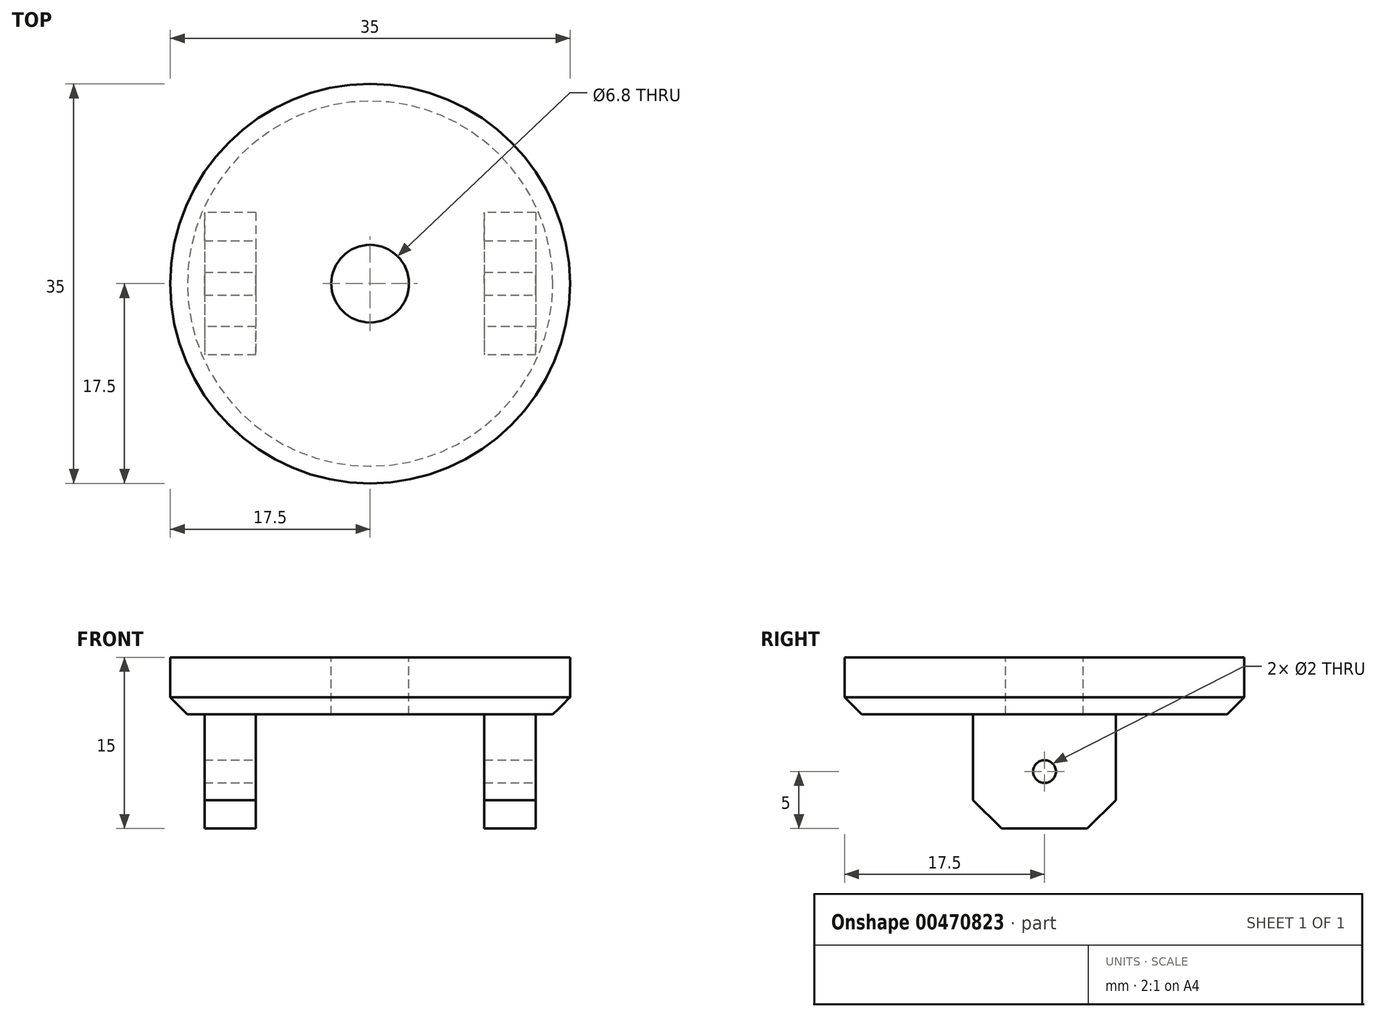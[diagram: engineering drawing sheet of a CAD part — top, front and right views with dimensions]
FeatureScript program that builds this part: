
annotation { "Feature Type Name" : "Feature", "Feature Type Description" : "" }
export const myFeature = defineFeature(function(context is Context, id is Id, definition is map)
    precondition{}
    {
        {
            var Q0;
            Q0=qCreatedBy(makeId("Top.planeOp"),FACE);
            var sketch = newSketch(context, id + "F0", { "sketchPlane" : qUnion([Q0])});
            skLineSegment(sketch, "E0.left", {"start": v(25, -7.7) * mm, "end": v(25, 7.7) * mm});
            skLineSegment(sketch, "E0.right", {"start": v(-25, -7.7) * mm, "end": v(-25, 7.7) * mm});
            skPoint(sketch, "E0.middle", {"position": v(0, 0) * mm});
            skEllipticalArc(sketch, "E1", {});
            skPoint(sketch, "E2.visualSharp", {"position": v(-25, 12.78) * mm});
            skArc(sketch, "E2.filletArc", {"start": v(-19.86, 15.83) * mm, "mid": v(-23.6, 12.5) * mm, "end": v(-25, 7.7) * mm});
            skArc(sketch, "E3.filletArc", {"start": v(-25, -7.7) * mm, "mid": v(-23.6, -12.5) * mm, "end": v(-19.86, -15.83) * mm});
            skEllipticalArc(sketch, "E4.trimOffspring", {});
            skPoint(sketch, "E5.visualSharp", {"position": v(25, 12.78) * mm});
            skArc(sketch, "E5.filletArc", {"start": v(25, 7.7) * mm, "mid": v(23.6, 12.5) * mm, "end": v(19.86, 15.83) * mm});
            skPoint(sketch, "E6.visualSharp", {"position": v(25, -12.78) * mm});
            skArc(sketch, "E6.filletArc", {"start": v(19.86, -15.83) * mm, "mid": v(23.6, -12.5) * mm, "end": v(25, -7.7) * mm});
            const initialGuessF0  = {"E1": [0, 0, 1, 0, 0.0325, 0.02, 4.054867696901255, 5.3699102638681255], "E4.trimOffspring": [0, 0, 1, 0, 0.0325, 0.02, 0.913275043311461, 2.2283176102783337]};
            skSetInitialGuess(sketch, initialGuessF0);
            skSolve(sketch);
        }
        {
            var Q0;
            Q0=makeQuery(id+"F0.imprint","IMPRINT",FACE,{"disambiguationData":[TD([[makeQuery(id+"F0.imprint","IMPRINT",EDGE,{"derivedFrom":sQuery(id+"F0.wireOp",EDGE,"E0.left")}),1.0]])]});
            extrude(context, id + "F1", {"entities" : qUnion([Q0]), "depth" : 5 * mm});
        }
        {
            var Q0;
            Q0=makeQuery(id+"F1.opExtrude","CAP_FACE",FACE,{"disambiguationData":[OSD([sQuery(id+"F0.wireOp",EDGE,"E0.left"),sQuery(id+"F0.wireOp",EDGE,"E0.right"),sQuery(id+"F0.wireOp",EDGE,"E1"),sQuery(id+"F0.wireOp",EDGE,"E2.filletArc"),sQuery(id+"F0.wireOp",EDGE,"E3.filletArc"),sQuery(id+"F0.wireOp",EDGE,"E4.trimOffspring"),sQuery(id+"F0.wireOp",EDGE,"E5.filletArc"),sQuery(id+"F0.wireOp",EDGE,"E6.filletArc")])],"isStart":true});
            var sketch = newSketch(context, id + "F2", { "sketchPlane" : qUnion([Q0])});
            skLineSegment(sketch, "E7.bottom", {"start": v(14.5, -6.25) * mm, "end": v(10, -6.25) * mm});
            skLineSegment(sketch, "E7.top", {"start": v(14.5, 6.25) * mm, "end": v(10, 6.25) * mm});
            skLineSegment(sketch, "E7.left", {"start": v(14.5, -6.25) * mm, "end": v(14.5, 6.25) * mm});
            skLineSegment(sketch, "E7.right", {"start": v(-14.5, -6.25) * mm, "end": v(-14.5, 6.25) * mm});
            skPoint(sketch, "E7.middle", {"position": v(0, 0) * mm});
            skLineSegment(sketch, "E8.left", {"start": v(10, -6.25) * mm, "end": v(10, 6.25) * mm});
            skLineSegment(sketch, "E8.right", {"start": v(-10, -6.25) * mm, "end": v(-10, 6.25) * mm});
            skLineSegment(sketch, "E9.trimOffspring", {"start": v(-10, 6.25) * mm, "end": v(-14.5, 6.25) * mm});
            skLineSegment(sketch, "E10.trimOffspring", {"start": v(-10, -6.25) * mm, "end": v(-14.5, -6.25) * mm});
            skSolve(sketch);
        }
        {
            var Q0;
            Q0=makeQuery(id+"F1.opExtrude","CAP_EDGE",EDGE,{"disambiguationData":[OSD([sQuery(id+"F0.wireOp",EDGE,"E1")])],"isStart":true});
            var Q1;
            Q1=makeQuery(id+"FL3o96M6EoHQmEN_1.opExtrude","CAP_FACE",FACE,{"disambiguationData":[OSD([sQuery(id+"F2.wireOp",EDGE,"E7.bottom"),sQuery(id+"F2.wireOp",EDGE,"E7.top"),sQuery(id+"F2.wireOp",EDGE,"E7.left"),sQuery(id+"F2.wireOp",EDGE,"E7.right")])],"isStart":false});
            chamfer(context, id + "F3", {"entities" : qUnion([Q0, Q1]), "width" : 1 * mm, "tangentPropagation" : true});
        }
        {
            var Q0;
            Q0 = qSketchRegion(id + "F2", true);
            extrude(context, id + "F4", {"entities" : qUnion([Q0]), "operationType" : NewBodyOperationType.ADD, "depth" : 10 * mm});
        }
        {
            var Q0;
            Q0=makeQuery(id+"F4.opExtrude","CAP_EDGE",EDGE,{"disambiguationData":[OSD([sQuery(id+"F2.wireOp",EDGE,"E9.trimOffspring")])],"isStart":false});
            var Q1;
            Q1=makeQuery(id+"F4.opExtrude","CAP_EDGE",EDGE,{"disambiguationData":[OSD([sQuery(id+"F2.wireOp",EDGE,"E7.top")])],"isStart":false});
            var Q2;
            Q2=makeQuery(id+"F4.opExtrude","CAP_EDGE",EDGE,{"disambiguationData":[OSD([sQuery(id+"F2.wireOp",EDGE,"E10.trimOffspring")])],"isStart":false});
            var Q3;
            Q3=makeQuery(id+"F4.opExtrude","CAP_EDGE",EDGE,{"disambiguationData":[OSD([sQuery(id+"F2.wireOp",EDGE,"E7.bottom")])],"isStart":false});
            chamfer(context, id + "F5", {"entities" : qUnion([Q0, Q1, Q2, Q3]), "width" : 2.5 * mm, "tangentPropagation" : true});
        }
        {
            var Q0;
            Q0=makeQuery(id+"F4.opExtrude","SWEPT_FACE",FACE,{"disambiguationData":[OSD([sQuery(id+"F2.wireOp",EDGE,"E7.left")])]});
            var sketch = newSketch(context, id + "F6", { "sketchPlane" : qUnion([Q0])});
            skCircle(sketch, "E11", {"center": v(0, -5) * mm, "radius": 1 * mm});
            skSolve(sketch);
        }
        {
            var Q0;
            Q0 = qSketchRegion(id + "F6", true);
            extrude(context, id + "F7", {"entities" : qUnion([Q0]), "operationType" : NewBodyOperationType.REMOVE, "endBound" : BoundingType.THROUGH_ALL, "oppositeDirection" : true, "depth" : 25 * mm});
        }
        {
            var Q0;
            Q0=makeQuery(id+"F1.opExtrude","CAP_FACE",FACE,{"disambiguationData":[OSD([sQuery(id+"F0.wireOp",EDGE,"E0.left"),sQuery(id+"F0.wireOp",EDGE,"E0.right"),sQuery(id+"F0.wireOp",EDGE,"E1"),sQuery(id+"F0.wireOp",EDGE,"E2.filletArc"),sQuery(id+"F0.wireOp",EDGE,"E3.filletArc"),sQuery(id+"F0.wireOp",EDGE,"E4.trimOffspring"),sQuery(id+"F0.wireOp",EDGE,"E5.filletArc"),sQuery(id+"F0.wireOp",EDGE,"E6.filletArc")])],"isStart":false});
            var sketch = newSketch(context, id + "F8", { "sketchPlane" : qUnion([Q0])});
            skCircle(sketch, "E12", {"center": v(0, 0) * mm, "radius": 17.5 * mm});
            skCircle(sketch, "E13", {"center": v(0, 0) * mm, "radius": 39.59 * mm});
            skSolve(sketch);
        }
        {
            var Q0;
            Q0=makeQuery(id+"F8.imprint","IMPRINT",FACE,{"disambiguationData":[TD([[makeQuery(id+"F8.imprint","IMPRINT",EDGE,{"derivedFrom":sQuery(id+"F8.wireOp",EDGE,"E12")}),-1.0]])]});
            var Q1;
            Q1=makeQuery(id+"F8.imprint","IMPRINT",FACE,{"disambiguationData":[TD([[makeQuery(id+"F8.imprint","IMPRINT",EDGE,{"derivedFrom":sQuery(id+"F8.wireOp",EDGE,"E13")}),1.0]])]});
            extrude(context, id + "F9", {"entities" : qUnion([Q0, Q1]), "operationType" : NewBodyOperationType.REMOVE, "oppositeDirection" : true, "depth" : 25 * mm});
        }
        {
            var Q0;
            Q0=makeQuery(id+"F9.boolean.opBoolean","INTERSECT",EDGE,{"derivedFrom":[makeQuery(id+"F1.opExtrude","CAP_FACE",FACE,{"disambiguationData":[OSD([sQuery(id+"F0.wireOp",EDGE,"E0.left"),sQuery(id+"F0.wireOp",EDGE,"E0.right"),sQuery(id+"F0.wireOp",EDGE,"E1"),sQuery(id+"F0.wireOp",EDGE,"E2.filletArc"),sQuery(id+"F0.wireOp",EDGE,"E3.filletArc"),sQuery(id+"F0.wireOp",EDGE,"E4.trimOffspring"),sQuery(id+"F0.wireOp",EDGE,"E5.filletArc"),sQuery(id+"F0.wireOp",EDGE,"E6.filletArc")])],"isStart":true}),makeQuery(id+"F9.opExtrude","SWEPT_FACE",FACE,{"disambiguationData":[OSD([sQuery(id+"F8.wireOp",EDGE,"E12")])]})]});
            chamfer(context, id + "F10", {"entities" : qUnion([Q0]), "width" : 1.5 * mm, "tangentPropagation" : true});
        }
        {
            var Q0;
            Q0=makeQuery(id+"F1.opExtrude","CAP_FACE",FACE,{"disambiguationData":[OSD([sQuery(id+"F0.wireOp",EDGE,"E0.left"),sQuery(id+"F0.wireOp",EDGE,"E0.right"),sQuery(id+"F0.wireOp",EDGE,"E1"),sQuery(id+"F0.wireOp",EDGE,"E2.filletArc"),sQuery(id+"F0.wireOp",EDGE,"E3.filletArc"),sQuery(id+"F0.wireOp",EDGE,"E4.trimOffspring"),sQuery(id+"F0.wireOp",EDGE,"E5.filletArc"),sQuery(id+"F0.wireOp",EDGE,"E6.filletArc")])],"isStart":false});
            var sketch = newSketch(context, id + "F11", { "sketchPlane" : qUnion([Q0])});
            skCircle(sketch, "E14", {"center": v(0, 0) * mm, "radius": 3.4 * mm});
            skSolve(sketch);
        }
        {
            var Q0;
            Q0=makeQuery(id+"F11.imprint","IMPRINT",FACE,{"disambiguationData":[TD([[makeQuery(id+"F11.imprint","IMPRINT",EDGE,{"derivedFrom":sQuery(id+"F11.wireOp",EDGE,"E14")}),1.0]])]});
            extrude(context, id + "F12", {"entities" : qUnion([Q0]), "operationType" : NewBodyOperationType.REMOVE, "oppositeDirection" : true, "depth" : 25 * mm});
        }
    });
